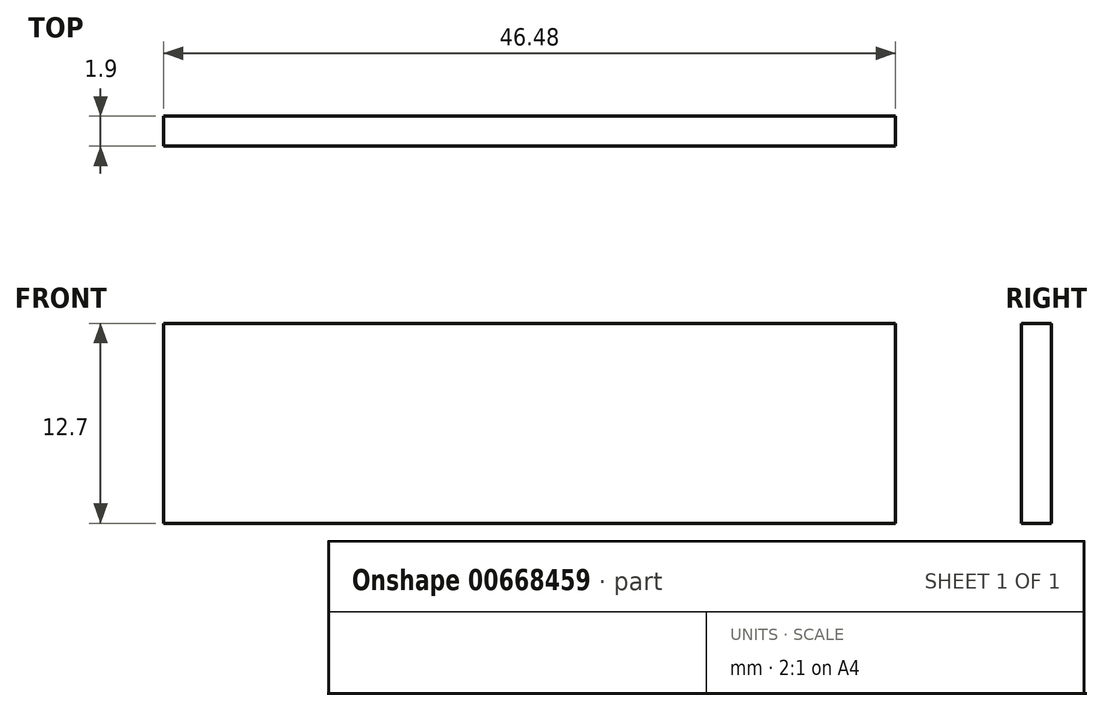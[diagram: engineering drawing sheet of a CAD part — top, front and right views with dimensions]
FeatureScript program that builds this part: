
annotation { "Feature Type Name" : "Feature", "Feature Type Description" : "" }
export const myFeature = defineFeature(function(context is Context, id is Id, definition is map)
    precondition{}
    {
        {
            var Q0;
            Q0=qCreatedBy(makeId("Front.planeOp"),FACE);
            var sketch = newSketch(context, id + "F0", { "sketchPlane" : qUnion([Q0])});
            skLineSegment(sketch, "E0.bottom", {"start": v(-15.93, 0) * mm, "end": v(-62.41, 0) * mm});
            skLineSegment(sketch, "E0.top", {"start": v(-15.93, -12.7) * mm, "end": v(-62.41, -12.7) * mm});
            skLineSegment(sketch, "E0.left", {"start": v(-15.93, 0) * mm, "end": v(-15.93, -12.7) * mm});
            skLineSegment(sketch, "E0.right", {"start": v(-62.41, 0) * mm, "end": v(-62.41, -12.7) * mm});
            skSolve(sketch);
        }
        {
            var Q0;
            Q0=makeQuery(id+"F0.imprint","IMPRINT",FACE,{"disambiguationData":[TD([[makeQuery(id+"F0.imprint","IMPRINT",EDGE,{"derivedFrom":sQuery(id+"F0.wireOp",EDGE,"E0.bottom")}),1.0]])]});
            extrude(context, id + "F1", {"entities" : qUnion([Q0]), "depth" : 1.9 * mm});
        }
    });
